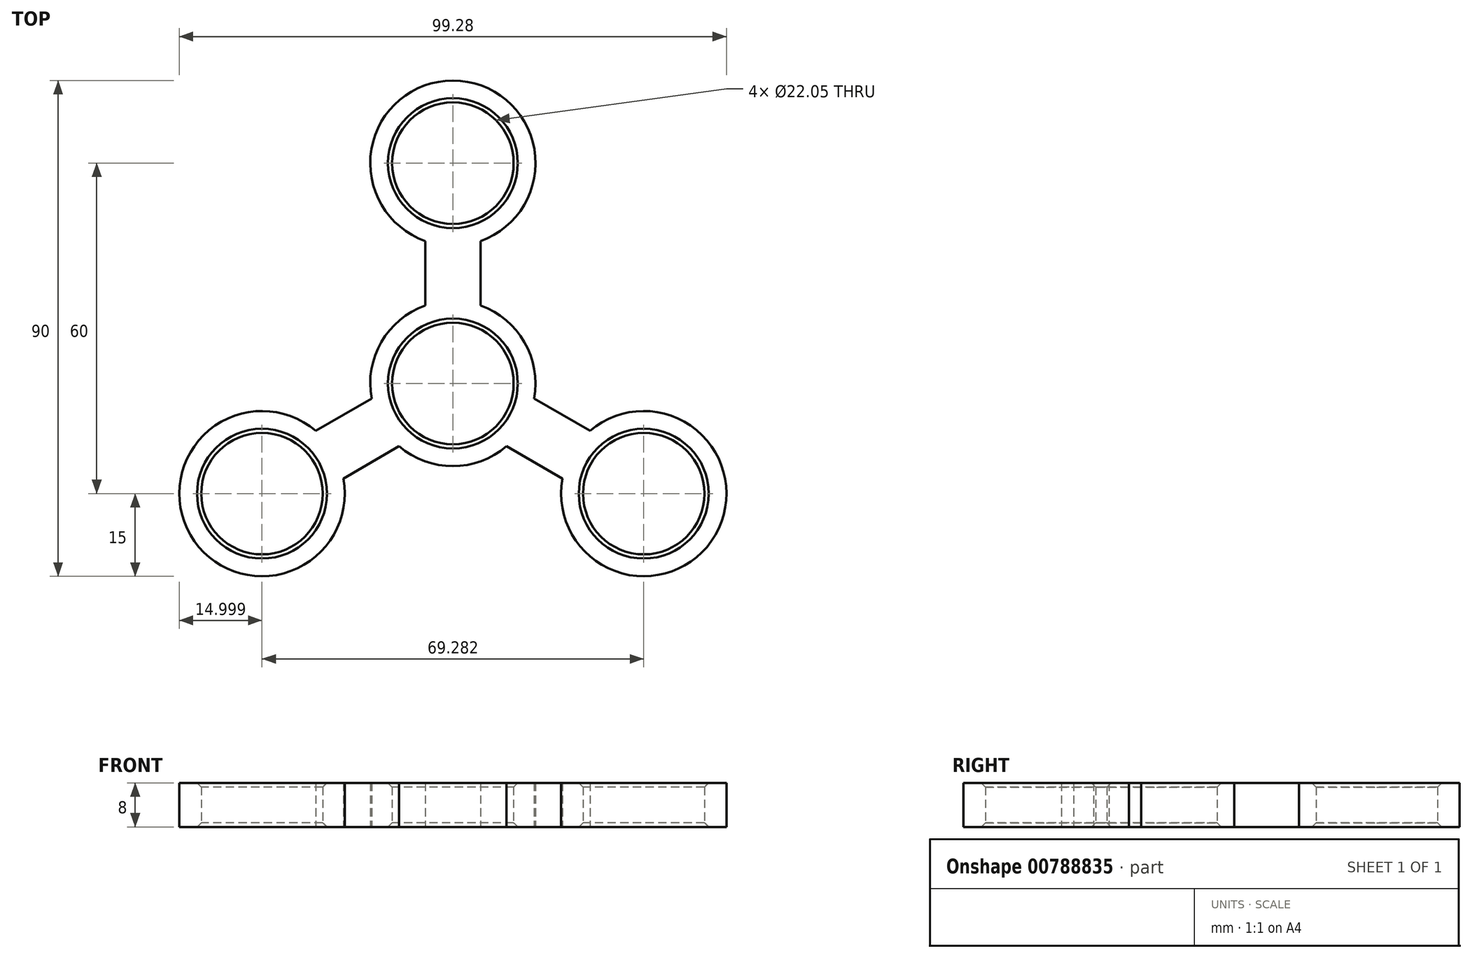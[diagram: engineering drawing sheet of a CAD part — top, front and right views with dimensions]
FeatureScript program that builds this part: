
annotation { "Feature Type Name" : "Feature", "Feature Type Description" : "" }
export const myFeature = defineFeature(function(context is Context, id is Id, definition is map)
    precondition{}
    {
        {
            var Q0;
            Q0=qCreatedBy(makeId("Top.planeOp"),FACE);
            var sketch = newSketch(context, id + "F0", { "sketchPlane" : qUnion([Q0])});
            skCircle(sketch, "E0", {"center": v(0, 0) * mm, "radius": 11.03 * mm});
            skLineSegment(sketch, "E1", {"start": v(0, 0) * mm, "end": v(0, 40) * mm});
            skCircle(sketch, "E2", {"center": v(0, 40) * mm, "radius": 11.03 * mm});
            skCircle(sketch, "E3", {"center": v(0, 0) * mm, "radius": 15 * mm});
            skCircle(sketch, "E4", {"center": v(0, 40) * mm, "radius": 15 * mm});
            skLineSegment(sketch, "E5.0", {"start": v(-5, 14.14) * mm, "end": v(-5, 25.86) * mm});
            skLineSegment(sketch, "E6.0", {"start": v(5, 14.14) * mm, "end": v(5, 25.86) * mm});
            skSolve(sketch);
        }
        {
            var Q0;
            Q0=makeQuery(id+"F0.imprint","IMPRINT",FACE,{"disambiguationData":[TD([[makeQuery(id+"F0.imprint","IMPRINT",EDGE,{"derivedFrom":sQuery(id+"F0.wireOp",EDGE,"E2")}),-1.0]])]});
            var Q1;
            {var subQ5=sQuery(id+"F0.wireOp",EDGE,"E6.0");Q1=makeQuery(id+"F0.imprint","IMPRINT",FACE,{"disambiguationData":[TD([[makeQuery(id+"F0.imprint","IMPRINT",EDGE,{"derivedFrom":subQ5}),1.0]])]});}
            var Q2;
            {var subQ5=sQuery(id+"F0.wireOp",EDGE,"E5.0");Q2=makeQuery(id+"F0.imprint","IMPRINT",FACE,{"disambiguationData":[TD([[makeQuery(id+"F0.imprint","IMPRINT",EDGE,{"derivedFrom":subQ5}),-1.0]])]});}
            var Q3;
            Q3=makeQuery(id+"F0.imprint","IMPRINT",FACE,{"disambiguationData":[TD([[makeQuery(id+"F0.imprint","IMPRINT",EDGE,{"derivedFrom":sQuery(id+"F0.wireOp",EDGE,"E0")}),-1.0]])]});
            extrude(context, id + "F1", {"entities" : qUnion([Q0, Q1, Q2, Q3]), "depth" : 8 * mm, "offsetDistance" : 25 * mm});
        }
        {
            var Q0;
            Q0=qCreatedBy(makeId("Front.planeOp"),FACE);
            var sketch = newSketch(context, id + "F2", { "sketchPlane" : qUnion([Q0])});
            skLineSegment(sketch, "E7", {"start": v(0, 0) * mm, "end": v(0, 46.65) * mm});
            skSolve(sketch);
        }
        {
            var Q0;
            Q0=makeQuery(id+"F1.opExtrude","SWEPT_BODY",BODY,{"disambiguationData":[OSD([sQuery(id+"F0.wireOp",EDGE,"E0"),sQuery(id+"F0.wireOp",EDGE,"E2"),sQuery(id+"F0.wireOp",EDGE,"E3"),sQuery(id+"F0.wireOp",EDGE,"E4"),sQuery(id+"F0.wireOp",EDGE,"E5.0"),sQuery(id+"F0.wireOp",EDGE,"E6.0")])]});
            var Q1;
            Q1=makeQuery(id+"F1.opExtrude","CAP_FACE",FACE,{"disambiguationData":[OSD([sQuery(id+"F0.wireOp",EDGE,"E0"),sQuery(id+"F0.wireOp",EDGE,"E2"),sQuery(id+"F0.wireOp",EDGE,"E3"),sQuery(id+"F0.wireOp",EDGE,"E4"),sQuery(id+"F0.wireOp",EDGE,"E5.0"),sQuery(id+"F0.wireOp",EDGE,"E6.0")])],"isStart":false});
            var Q2;
            Q2=sQuery(id+"F2.wireOp",EDGE,"E7");
            circularPattern(context, id + "F3", {"operationType" : NewBodyOperationType.ADD, "entities" : qUnion([Q0]), "axis" : qUnion([Q2]), "angle" : 360 * degree, "instanceCount" : 3, "equalSpace" : true});
        }
        {
            var Q0;
            Q0=makeQuery(id+"F1.opExtrude","CAP_EDGE",EDGE,{"disambiguationData":[OSD([sQuery(id+"F0.wireOp",EDGE,"E2")])],"isStart":false});
            var Q1;
            Q1=makeQuery(id+"F1.opExtrude","CAP_EDGE",EDGE,{"disambiguationData":[OSD([sQuery(id+"F0.wireOp",EDGE,"E0")])],"isStart":false});
            var Q2;
            Q2=makeQuery(id+"F3.opPattern","COPY",EDGE,{"derivedFrom":makeQuery(id+"F1.opExtrude","CAP_EDGE",EDGE,{"disambiguationData":[OSD([sQuery(id+"F0.wireOp",EDGE,"E2")])],"isStart":false}),"instanceName":"1"});
            var Q3;
            Q3=makeQuery(id+"F3.opPattern","COPY",EDGE,{"derivedFrom":makeQuery(id+"F1.opExtrude","CAP_EDGE",EDGE,{"disambiguationData":[OSD([sQuery(id+"F0.wireOp",EDGE,"E2")])],"isStart":false}),"instanceName":"2"});
            var Q4;
            Q4=makeQuery(id+"F3.opPattern","COPY",EDGE,{"derivedFrom":makeQuery(id+"F1.opExtrude","CAP_EDGE",EDGE,{"disambiguationData":[OSD([sQuery(id+"F0.wireOp",EDGE,"E2")])],"isStart":true}),"instanceName":"1"});
            var Q5;
            Q5=makeQuery(id+"F1.opExtrude","CAP_EDGE",EDGE,{"disambiguationData":[OSD([sQuery(id+"F0.wireOp",EDGE,"E0")])],"isStart":true});
            var Q6;
            Q6=makeQuery(id+"F3.opPattern","COPY",EDGE,{"derivedFrom":makeQuery(id+"F1.opExtrude","CAP_EDGE",EDGE,{"disambiguationData":[OSD([sQuery(id+"F0.wireOp",EDGE,"E2")])],"isStart":true}),"instanceName":"2"});
            var Q7;
            Q7=makeQuery(id+"F1.opExtrude","CAP_EDGE",EDGE,{"disambiguationData":[OSD([sQuery(id+"F0.wireOp",EDGE,"E2")])],"isStart":true});
            chamfer(context, id + "F4", {"entities" : qUnion([Q0, Q1, Q2, Q3, Q4, Q5, Q6, Q7]), "width" : 0.76 * mm, "tangentPropagation" : true});
        }
    });
